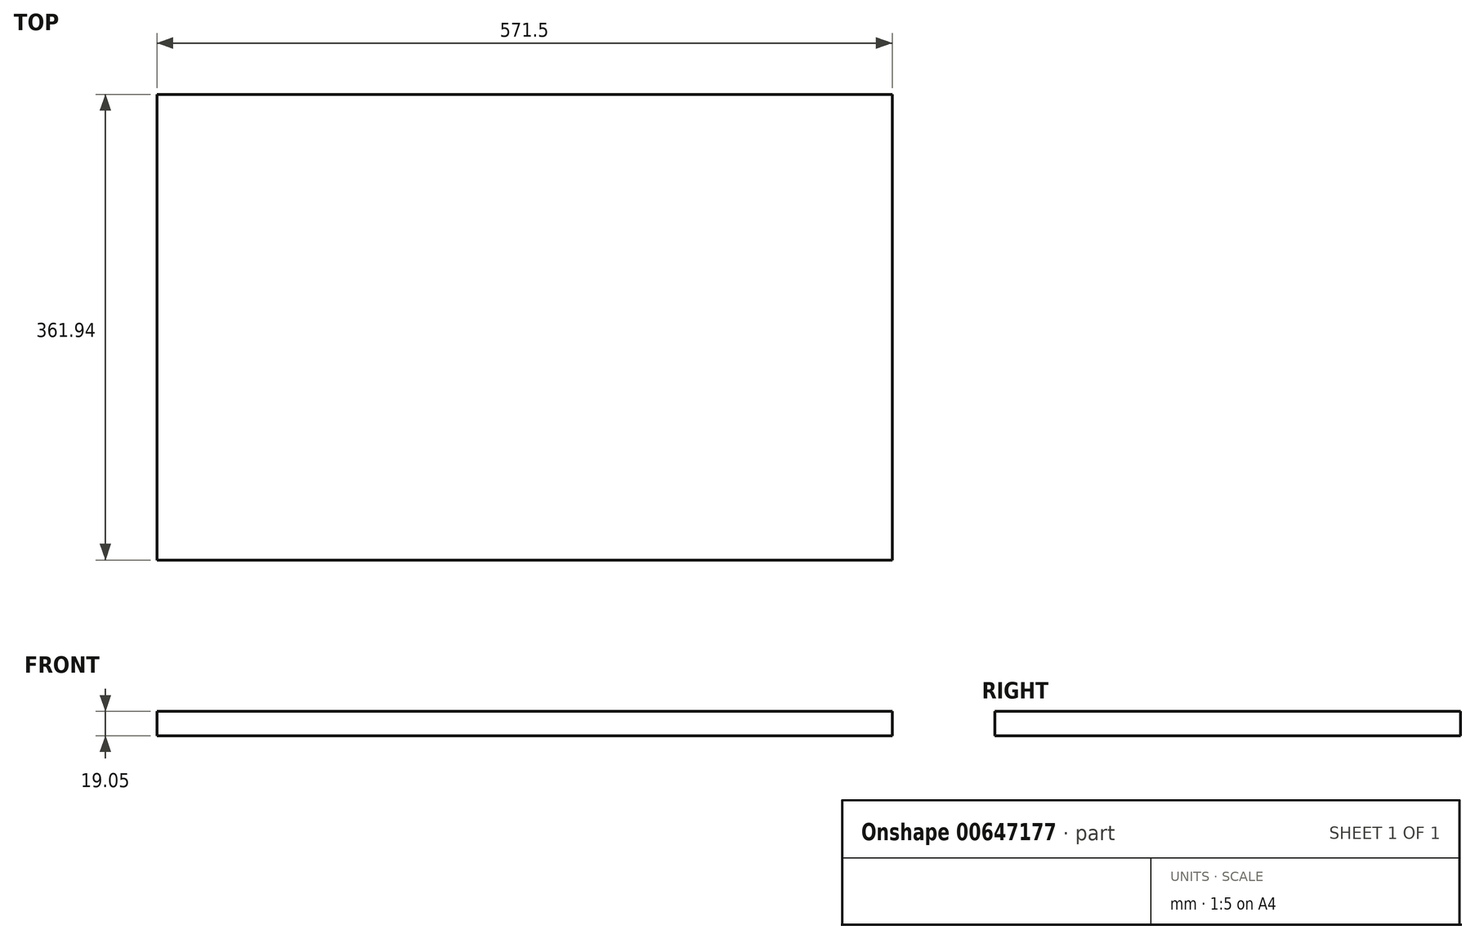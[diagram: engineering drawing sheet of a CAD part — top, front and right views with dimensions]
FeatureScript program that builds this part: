
annotation { "Feature Type Name" : "Feature", "Feature Type Description" : "" }
export const myFeature = defineFeature(function(context is Context, id is Id, definition is map)
    precondition{}
    {
        {
            var Q0;
            Q0=qCreatedBy(makeId("Top.planeOp"),FACE);
            var sketch = newSketch(context, id + "F0", { "sketchPlane" : qUnion([Q0])});
            skLineSegment(sketch, "E0.bottom", {"start": v(-285.75, 180.97) * mm, "end": v(285.75, 180.97) * mm});
            skLineSegment(sketch, "E0.top", {"start": v(-285.75, -180.98) * mm, "end": v(285.75, -180.98) * mm});
            skLineSegment(sketch, "E0.left", {"start": v(-285.75, 180.97) * mm, "end": v(-285.75, -180.98) * mm});
            skLineSegment(sketch, "E0.right", {"start": v(285.75, 180.97) * mm, "end": v(285.75, -180.98) * mm});
            skPoint(sketch, "E0.middle", {"position": v(0, 0) * mm});
            skSolve(sketch);
        }
        {
            var Q0;
            Q0=makeQuery(id+"F0.imprint","IMPRINT",FACE,{"disambiguationData":[TD([[makeQuery(id+"F0.imprint","IMPRINT",EDGE,{"derivedFrom":sQuery(id+"F0.wireOp",EDGE,"E0.bottom")}),-1.0]])]});
            extrude(context, id + "F1", {"entities" : qUnion([Q0]), "depth" : 19.05 * mm, "offsetDistance" : 25.4 * mm});
        }
    });
